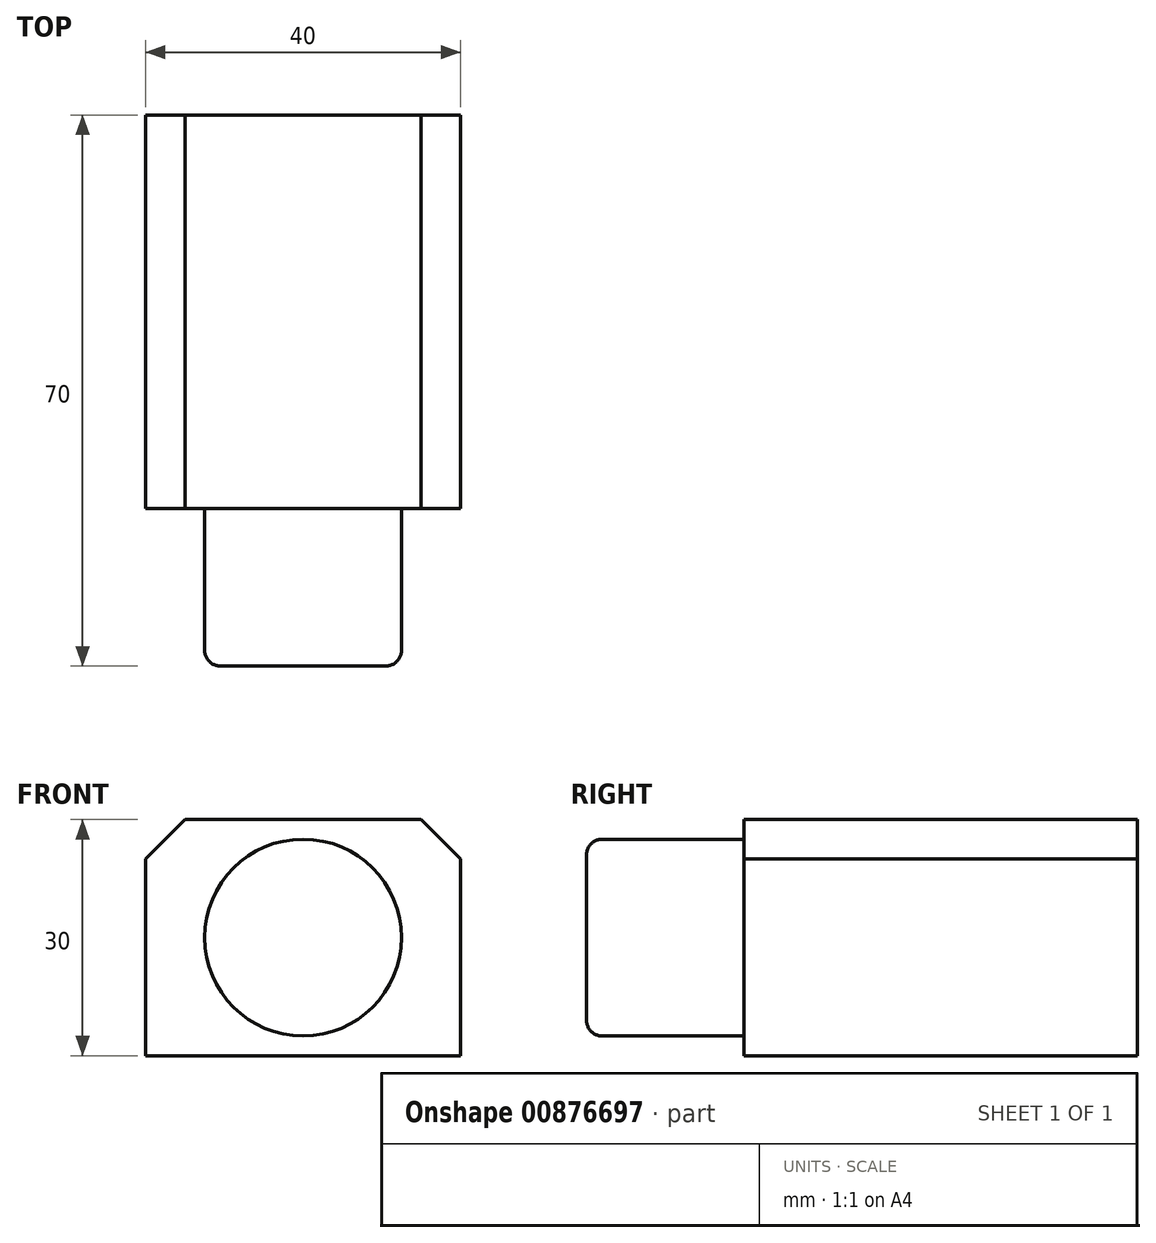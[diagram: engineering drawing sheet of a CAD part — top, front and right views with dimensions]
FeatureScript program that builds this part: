
annotation { "Feature Type Name" : "Feature", "Feature Type Description" : "" }
export const myFeature = defineFeature(function(context is Context, id is Id, definition is map)
    precondition{}
    {
        {
            var Q0;
            Q0=qCreatedBy(makeId("Front.planeOp"),FACE);
            var sketch = newSketch(context, id + "F0", { "sketchPlane" : qUnion([Q0])});
            skLineSegment(sketch, "E0.bottom", {"start": v(20, 15) * mm, "end": v(-20, 15) * mm});
            skLineSegment(sketch, "E0.top", {"start": v(20, -15) * mm, "end": v(-20, -15) * mm});
            skLineSegment(sketch, "E0.left", {"start": v(20, 15) * mm, "end": v(20, -15) * mm});
            skLineSegment(sketch, "E0.right", {"start": v(-20, 15) * mm, "end": v(-20, -15) * mm});
            skPoint(sketch, "E0.middle", {"position": v(0, 0) * mm});
            skSolve(sketch);
        }
        {
            var Q0;
            Q0=makeQuery(id+"F0.imprint","IMPRINT",FACE,{"disambiguationData":[TD([[makeQuery(id+"F0.imprint","IMPRINT",EDGE,{"derivedFrom":sQuery(id+"F0.wireOp",EDGE,"E0.bottom")}),1.0]])]});
            extrude(context, id + "F1", {"entities" : qUnion([Q0]), "depth" : 50 * mm, "offsetDistance" : 25 * mm});
        }
        {
            var Q0;
            Q0=makeQuery(id+"F1.opExtrude","CAP_FACE",FACE,{"disambiguationData":[OSD([sQuery(id+"F0.wireOp",EDGE,"E0.bottom"),sQuery(id+"F0.wireOp",EDGE,"E0.top"),sQuery(id+"F0.wireOp",EDGE,"E0.left"),sQuery(id+"F0.wireOp",EDGE,"E0.right")])],"isStart":false});
            var sketch = newSketch(context, id + "F2", { "sketchPlane" : qUnion([Q0])});
            skCircle(sketch, "E1", {"center": v(0, 0) * mm, "radius": 12.5 * mm});
            skSolve(sketch);
        }
        {
            var Q0;
            Q0=makeQuery(id+"F2.imprint","IMPRINT",FACE,{"disambiguationData":[TD([[makeQuery(id+"F2.imprint","IMPRINT",EDGE,{"derivedFrom":sQuery(id+"F2.wireOp",EDGE,"E1")}),1.0]])]});
            extrude(context, id + "F3", {"entities" : qUnion([Q0]), "operationType" : NewBodyOperationType.ADD, "depth" : 20 * mm, "offsetDistance" : 25 * mm});
        }
        {
            var Q0;
            Q0=makeQuery(id+"F3.opExtrude","CAP_EDGE",EDGE,{"disambiguationData":[OSD([sQuery(id+"F2.wireOp",EDGE,"E1")])],"isStart":false});
            fillet(context, id + "F4", {"entities" : qUnion([Q0]), "radius" : 2 * mm, "tangentPropagation" : true, "allowEdgeOverflow" : false});
        }
        {
            var Q0;
            Q0=makeQuery(id+"F1.opExtrude","SWEPT_EDGE",EDGE,{"disambiguationData":[OSD([sQuery(id+"F0.wireOp",EDGE,"E0.bottom"),sQuery(id+"F0.wireOp",EDGE,"E0.right")])]});
            var Q1;
            Q1=makeQuery(id+"F1.opExtrude","SWEPT_EDGE",EDGE,{"disambiguationData":[OSD([sQuery(id+"F0.wireOp",EDGE,"E0.bottom"),sQuery(id+"F0.wireOp",EDGE,"E0.left")])]});
            chamfer(context, id + "F5", {"entities" : qUnion([Q0, Q1]), "width" : 5 * mm, "tangentPropagation" : true});
        }
    });
